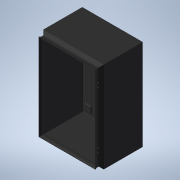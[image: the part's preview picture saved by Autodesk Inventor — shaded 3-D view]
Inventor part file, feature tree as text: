
AUTODESK INVENTOR PART (.ipt)
format: ipt  version: 2021 (Build 250183000, 183)  size: 907,264 bytes
history: native  units: mm
features: other x56, sketch x44, extrude x20, revolve x20, hole x4
ambient origin geometry x8: Origin, YZ Plane, XZ Plane, XY Plane, X Axis, Y Axis, Z Axis, Center Point
bodies: Solid1 (feature_tree)
feature tree (144):
  extrude  "Extrusion1"  Depth=300.0mm TaperAngle=0.0deg
  extrude  "Extrusion2"  Depth=300.0mm TaperAngle=0.0deg
  extrude  "Extrusion3"  Depth=3.25mm TaperAngle=0.0deg
  extrude  "Extrusion4"  Depth=3.25mm TaperAngle=0.0deg
  extrude  "Extrusion5"  Depth=15.297mm TaperAngle=0.0deg
  extrude  "Extrusion6"  Depth=15.297mm TaperAngle=0.0deg
  extrude  "Extrusion7"  Depth=15.297mm TaperAngle=0.0deg
  extrude  "Extrusion8"  Depth=15.297mm TaperAngle=0.0deg
  extrude  "Extrusion9"  TaperAngle=90.0deg  [1 undecoded]
  extrude  "Extrusion10"  TaperAngle=90.0deg  [1 undecoded]
  extrude  "Extrusion11"  TaperAngle=90.0deg  [1 undecoded]
  extrude  "Extrusion12"  TaperAngle=90.0deg  [1 undecoded]
  extrude  "Extrusion13"  TaperAngle=90.0deg  [1 undecoded]
  extrude  "Extrusion14"  TaperAngle=90.0deg  [1 undecoded]
  extrude  "Extrusion15"  TaperAngle=90.0deg  [1 undecoded]
  extrude  "Extrusion16"  TaperAngle=90.0deg  [1 undecoded]
  revolve  "Revolution1"  Angle=360.0deg
  revolve  "Revolution2"  Angle=360.0deg
  revolve  "Revolution3"  [1 undecoded]
  revolve  "Revolution4"  [1 undecoded]
  revolve  "Revolution5"  [1 undecoded]
  revolve  "Revolution6"  [1 undecoded]
  revolve  "Revolution7"  [1 undecoded]
  revolve  "Revolution8"  [1 undecoded]
  revolve  "Revolution9"  [1 undecoded]
  revolve  "Revolution10"  [1 undecoded]
  revolve  "Revolution11"  [1 undecoded]
  revolve  "Revolution12"  [1 undecoded]
  revolve  "Revolution13"  [1 undecoded]
  revolve  "Revolution14"  [1 undecoded]
  revolve  "Revolution15"  [1 undecoded]
  revolve  "Revolution16"  [1 undecoded]
  hole  "Hole1"  [1 undecoded]
  hole  "Hole2"  [1 undecoded]
  hole  "Hole3"  [1 undecoded]
  hole  "Hole4"  [1 undecoded]
  revolve  "Revolution17"  [1 undecoded]
  revolve  "Revolution18"  [1 undecoded]
  revolve  "Revolution19"  [1 undecoded]
  revolve  "Revolution20"  [1 undecoded]
  extrude  "Extrusion17"  [1 undecoded]
  extrude  "Extrusion18"  [1 undecoded]
  extrude  "Extrusion19"  [1 undecoded]
  extrude  "Extrusion20"  [1 undecoded]
  other  "GEHAEUSE_XY"
  other  "GEHAEUSE_YZ"
  other  "GEHAEUSE_ZX"
  other  "GEHAEUSE_X"
  other  "GEHAEUSE_Y"
  other  "GEHAEUSE_Z"
  other  "GEHAEUSE_Center"
  other  "to_HINGE_1_XY"
  other  "to_HINGE_1_YZ"
  other  "to_HINGE_1_ZX"
  other  "to_HINGE_1_X"
  other  "to_HINGE_1_Y"
  other  "to_HINGE_1_Z"
  other  "to_HINGE_1_Center"
  other  "to_HINGE_2_XY"
  other  "to_HINGE_2_YZ"
  other  "to_HINGE_2_ZX"
  other  "to_HINGE_2_X"
  other  "to_HINGE_2_Y"
  other  "to_HINGE_2_Z"
  other  "to_HINGE_2_Center"
  other  "to_L_Winkel_XY"
  other  "to_L_Winkel_YZ"
  other  "to_L_Winkel_ZX"
  other  "to_L_Winkel_X"
  other  "to_L_Winkel_Y"
  other  "to_L_Winkel_Z"
  other  "to_L_Winkel_Center"
  other  "to_L_Winkel_Bottom_XY"
  other  "to_L_Winkel_Bottom_YZ"
  other  "to_L_Winkel_Bottom_ZX"
  other  "to_L_Winkel_Bottom_X"
  other  "to_L_Winkel_Bottom_Y"
  other  "to_L_Winkel_Bottom_Z"
  other  "to_L_Winkel_Bottom_Center"
  other  "to_L_Winkel_Top_XY"
  other  "to_L_Winkel_Top_YZ"
  other  "to_L_Winkel_Top_ZX"
  other  "to_L_Winkel_Top_X"
  other  "to_L_Winkel_Top_Y"
  other  "to_L_Winkel_Top_Z"
  other  "to_L_Winkel_Top_Center"
  other  "to_L_Winkel_1_XY"
  other  "to_L_Winkel_1_YZ"
  other  "to_L_Winkel_1_ZX"
  other  "to_L_Winkel_1_X"
  other  "to_L_Winkel_1_Y"
  other  "to_L_Winkel_1_Z"
  other  "to_L_Winkel_1_Center"
  other  "to_MP_XY"
  other  "to_MP_YZ"
  other  "to_MP_ZX"
  other  "to_MP_X"
  other  "to_MP_Y"
  other  "to_MP_Z"
  other  "to_MP_Center"
  sketch  "Skizze_2"  dims[d4=200.0mm d5=0.0mm d6=300.0mm d7=0.0mm]
  sketch  "Sketch_1"  dims[d0=200.0mm d1=0.0mm d2=300.0mm d3=0.0mm]
  sketch  "Sketch_37"  dims[d44=90.0deg d45=90.0deg]
  sketch  "Sketch_38"  dims[d46=90.0deg d47=90.0deg]
  sketch  "Sketch_2"  dims[d8=3.25mm d9=0.0mm d10=3.25mm d11=0.0mm]
  sketch  "Sketch_9"  dims[d12=3.25mm d13=0.0mm d14=3.25mm d15=0.0mm]
  sketch  "Sketch_10"  dims[d16=15.297mm d17=0.0mm d18=15.297mm d19=0.0mm]
  sketch  "Sketch_11"  dims[d20=15.297mm d21=0.0mm d22=15.297mm d23=0.0mm]
  sketch  "Sketch_30"  dims[d24=15.297mm d25=0.0mm d26=15.297mm d27=0.0mm]
  sketch  "Sketch_31"  dims[d28=15.297mm d29=0.0mm d30=15.297mm d31=0.0mm]
  sketch  "Sketch_32"  dims[d32=90.0deg d33=90.0deg]
  sketch  "Sketch_33"  dims[d34=90.0deg d35=90.0deg]
  sketch  "Sketch_43"  dims[d48=3.2mm d49=6.0mm d50=4.0mm d51=2.0mm d52=90.0deg d53=1.25mm d54=0.0mm]
  sketch  "Sketch_44"  dims[d55=3.2mm d56=6.0mm d57=4.0mm d58=2.0mm d59=90.0deg d60=1.25mm d61=0.0mm]
  sketch  "Sketch_45"  dims[d62=3.2mm d63=6.0mm d64=4.0mm d65=2.0mm d66=90.0deg d67=1.25mm d68=0.0mm]
  sketch  "Sketch_46"  dims[d69=3.2mm d70=6.0mm d71=4.0mm d72=2.0mm d73=90.0deg d74=1.25mm d75=0.0mm d76=360.0deg]
  sketch  "Sketch_47"  dims[d77=360.0deg d78=360.0deg]
  sketch  "Sketch_48"  dims[d79=360.0deg d80=1.2mm d81=0.0mm]
  sketch  "Sketch_49"  dims[d82=1.2mm d83=0.0mm d84=1.2mm d85=0.0mm]
  sketch  "Sketch_50"  dims[d86=1.2mm d87=0.0mm d88=0.0mm d89=0.0mm d90=0.0mm d91=0.0mm]
  sketch  "Sketch_51"
  sketch  "Sketch_52"
  sketch  "Sketch_53"
  sketch  "Sketch_54"
  sketch  "Sketch_55"
  sketch  "Sketch_56"
  sketch  "Sketch_57"
  sketch  "Sketch_58"
  sketch  "Sketch_59"
  sketch  "Sketch_60"
  sketch  "Sketch_61"
  sketch  "Sketch_62"
  sketch  "Sketch33"  dims[d36=90.0deg d37=90.0deg]
  sketch  "Sketch34"  dims[d38=90.0deg d39=90.0deg]
  sketch  "Sketch35"  dims[d40=90.0deg d41=90.0deg]
  sketch  "Sketch36"  dims[d42=90.0deg d43=90.0deg]
  sketch  "Sketch_75"
  sketch  "Sketch_76"
  sketch  "Sketch_77"
  sketch  "Sketch_78"
  sketch  "Sketch_79"
  sketch  "Sketch_80"
  sketch  "Sketch_81"
  sketch  "Sketch_82"
note: 34 required parameter values undecoded (feature->parameter linkage not recoverable at this tier; creation-order binding heuristic only, values carry confidence <= 0.55)